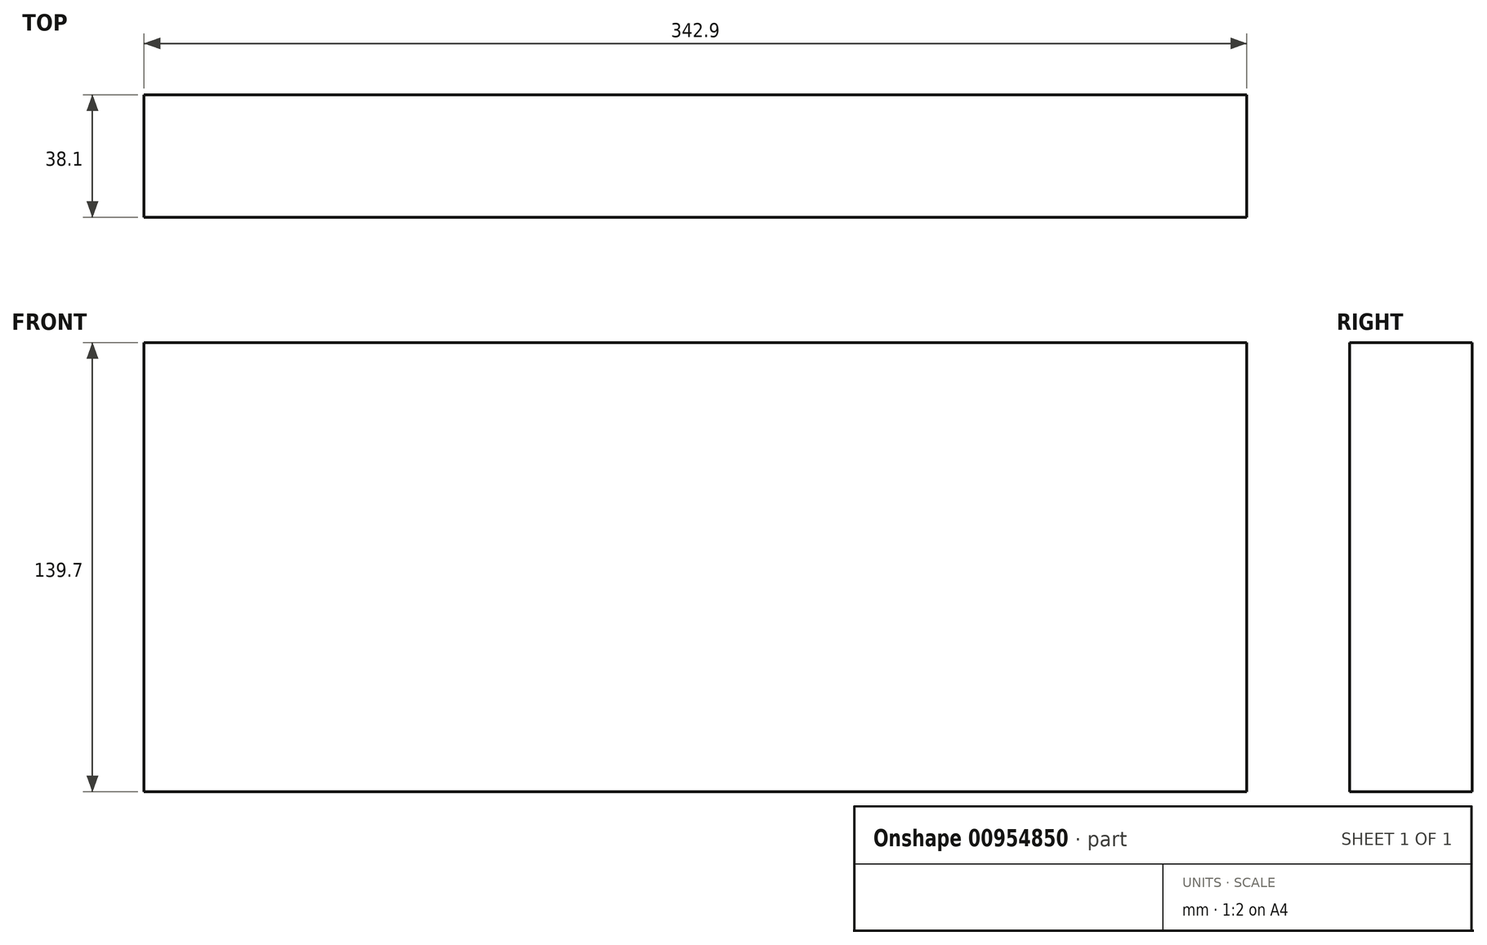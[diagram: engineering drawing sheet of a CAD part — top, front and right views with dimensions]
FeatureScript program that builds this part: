
annotation { "Feature Type Name" : "Feature", "Feature Type Description" : "" }
export const myFeature = defineFeature(function(context is Context, id is Id, definition is map)
    precondition{}
    {
        {
            var Q0;
            Q0=qCreatedBy(makeId("Right.planeOp"),FACE);
            var sketch = newSketch(context, id + "F0", { "sketchPlane" : qUnion([Q0])});
            skLineSegment(sketch, "E0.bottom", {"start": v(-19.05, 69.85) * mm, "end": v(19.05, 69.85) * mm});
            skLineSegment(sketch, "E0.top", {"start": v(-19.05, -69.85) * mm, "end": v(19.05, -69.85) * mm});
            skLineSegment(sketch, "E0.left", {"start": v(-19.05, 69.85) * mm, "end": v(-19.05, -69.85) * mm});
            skLineSegment(sketch, "E0.right", {"start": v(19.05, 69.85) * mm, "end": v(19.05, -69.85) * mm});
            skPoint(sketch, "E1", {"position": v(0, 69.85) * mm});
            skPoint(sketch, "E2", {"position": v(-19.05, 0) * mm});
            skSolve(sketch);
        }
        {
            var Q0;
            Q0=qSketchRegion(id+"F0",true);
            extrude(context, id + "F1", {"entities" : qUnion([Q0]), "endBound" : BoundingType.SYMMETRIC, "depth" : 342.9 * mm, "offsetDistance" : 25.4 * mm, "hasSecondDirection" : true, "secondDirectionOppositeDirection" : true, "secondDirectionDepth" : 609.6 * mm});
        }
    });
